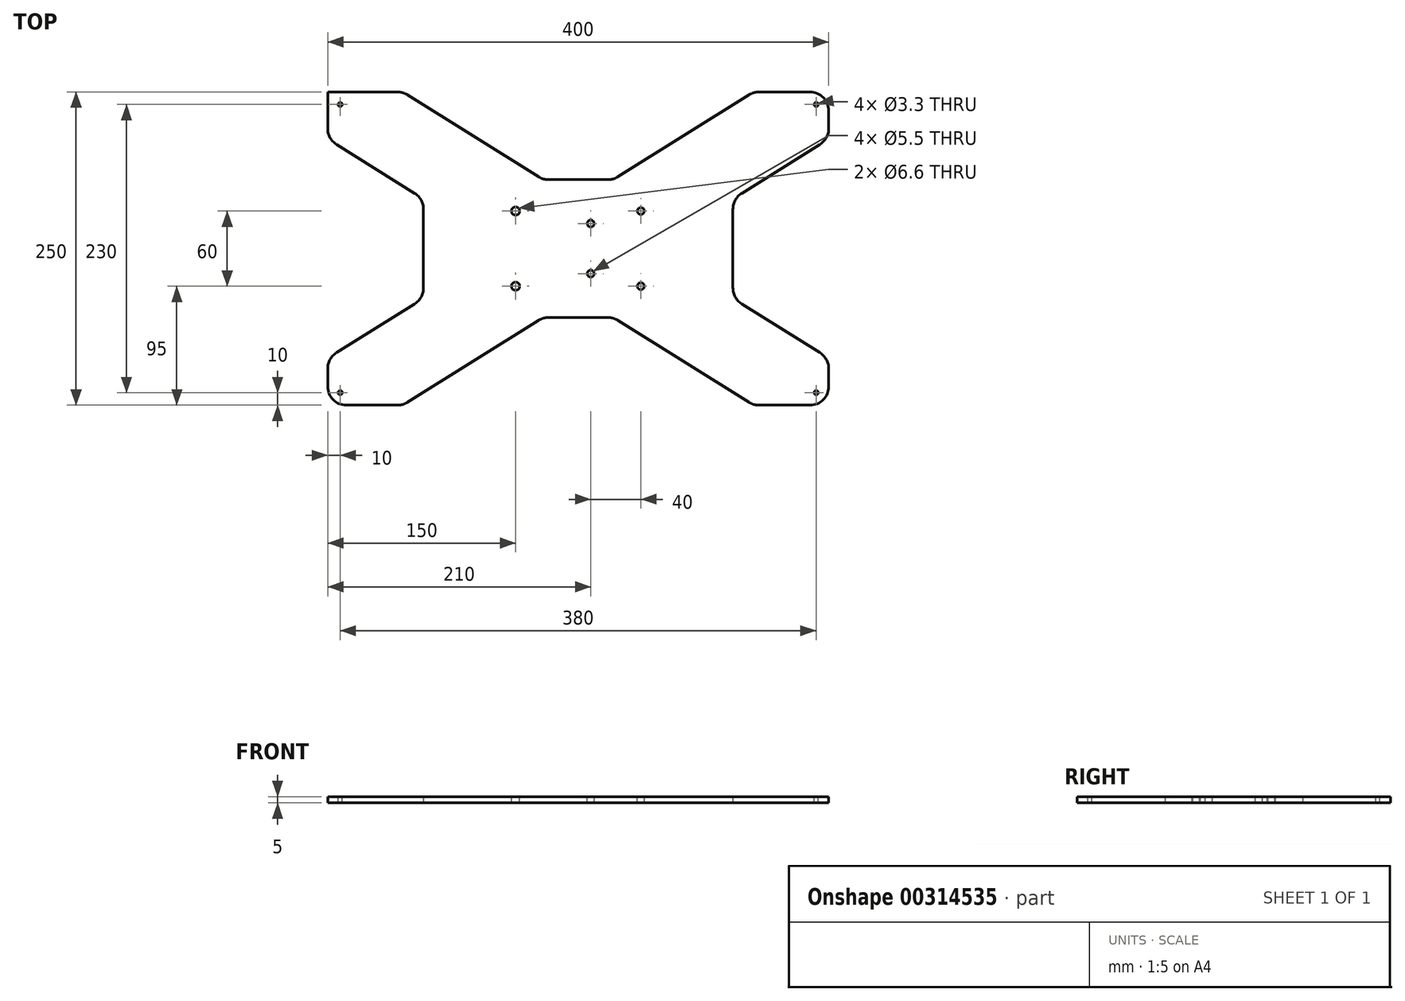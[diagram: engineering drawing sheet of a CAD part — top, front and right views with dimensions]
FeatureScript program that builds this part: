
annotation { "Feature Type Name" : "Feature", "Feature Type Description" : "" }
export const myFeature = defineFeature(function(context is Context, id is Id, definition is map)
    precondition{}
    {
        {
            var Q0;
            Q0=qCreatedBy(makeId("Top.planeOp"),FACE);
            var sketch = newSketch(context, id + "F0", { "sketchPlane" : qUnion([Q0])});
            skLineSegment(sketch, "E0.bottom", {"start": v(200, -125) * mm, "end": v(140, -125) * mm});
            skLineSegment(sketch, "E0.top", {"start": v(200, 125) * mm, "end": v(140, 125) * mm});
            skLineSegment(sketch, "E0.left", {"start": v(200, -125) * mm, "end": v(200, -87.5) * mm});
            skLineSegment(sketch, "E0.right", {"start": v(-200, -125) * mm, "end": v(-200, -87.5) * mm});
            skPoint(sketch, "E0.middle", {"position": v(0, 0) * mm});
            skLineSegment(sketch, "E1.bottom", {"start": v(-28, -55) * mm, "end": v(28, -55) * mm});
            skLineSegment(sketch, "E1.left", {"start": v(-123.5, -39.69) * mm, "end": v(-123.5, 39.69) * mm});
            skLineSegment(sketch, "E1.right", {"start": v(123.5, -39.69) * mm, "end": v(123.5, 39.69) * mm});
            skLineSegment(sketch, "E2", {"start": v(-200, -125) * mm, "end": v(200, 125) * mm, "construction": true});
            skLineSegment(sketch, "E3", {"start": v(-200, 125) * mm, "end": v(200, -125) * mm, "construction": true});
            skLineSegment(sketch, "E4.bottom", {"start": v(-200, -125) * mm, "end": v(-140, -125) * mm});
            skLineSegment(sketch, "E5.MirrorCS", {"start": v(-200, 125) * mm, "end": v(-140, 125) * mm});
            skLineSegment(sketch, "E6.MirrorCS", {"start": v(-200, 125) * mm, "end": v(-200, 87.5) * mm});
            skLineSegment(sketch, "E7", {"start": v(-200, 87.5) * mm, "end": v(-123.5, 39.69) * mm});
            skLineSegment(sketch, "E8", {"start": v(-140, 125) * mm, "end": v(-28, 55) * mm});
            skLineSegment(sketch, "E9", {"start": v(-200, -87.5) * mm, "end": v(-123.5, -39.69) * mm});
            skLineSegment(sketch, "E10", {"start": v(-140, -125) * mm, "end": v(-28, -55) * mm});
            skPoint(sketch, "E11.MirrorCS.end.orphan", {"position": v(-140, 87.5) * mm});
            skPoint(sketch, "E12.MirrorCS.end.orphan", {"position": v(140, 87.5) * mm});
            skPoint(sketch, "E4.top.end.orphan", {"position": v(-140, -87.5) * mm});
            skPoint(sketch, "E13.MirrorCS.end.orphan", {"position": v(140, -87.5) * mm});
            skLineSegment(sketch, "E14.trimOffspring", {"start": v(123.5, 39.69) * mm, "end": v(200, 87.5) * mm});
            skLineSegment(sketch, "E15.trimOffspring", {"start": v(123.5, -39.69) * mm, "end": v(200, -87.5) * mm});
            skLineSegment(sketch, "E16.trimOffspring", {"start": v(28, 55) * mm, "end": v(140, 125) * mm});
            skLineSegment(sketch, "E17.trimOffspring", {"start": v(28, -55) * mm, "end": v(140, -125) * mm});
            skLineSegment(sketch, "E18.trimOffspring", {"start": v(-200, 87.5) * mm, "end": v(-200, 125) * mm});
            skLineSegment(sketch, "E19.trimOffspring", {"start": v(-140, 125) * mm, "end": v(-200, 125) * mm});
            skLineSegment(sketch, "E20.trimOffspring", {"start": v(200, 87.5) * mm, "end": v(200, 125) * mm});
            skLineSegment(sketch, "E21.trimOffspring", {"start": v(-140, -125) * mm, "end": v(-200, -125) * mm});
            skPoint(sketch, "E22.orphan", {"position": v(123.5, 55) * mm});
            skLineSegment(sketch, "E23.trimOffspring", {"start": v(-28, 55) * mm, "end": v(28, 55) * mm});
            skPoint(sketch, "E24.orphan", {"position": v(-123.5, 55) * mm});
            skPoint(sketch, "E25.orphan", {"position": v(-123.5, -55) * mm});
            skPoint(sketch, "E26.orphan", {"position": v(123.5, -55) * mm});
            skSolve(sketch);
        }
        {
            var Q0;
            Q0 = qSketchRegion(id + "F0", true);
            extrude(context, id + "F1", {"entities" : qUnion([Q0]), "depth" : 5 * mm});
        }
        {
            var Q0;
            Q0=makeQuery(id+"F1.opExtrude","CAP_FACE",FACE,{"disambiguationData":[OSD([sQuery(id+"F0.wireOp",EDGE,"E1.bottom"),sQuery(id+"F0.wireOp",EDGE,"E1.left"),sQuery(id+"F0.wireOp",EDGE,"E1.right"),sQuery(id+"F0.wireOp",EDGE,"E0.right"),sQuery(id+"F0.wireOp",EDGE,"E0.top"),sQuery(id+"F0.wireOp",EDGE,"E0.left"),sQuery(id+"F0.wireOp",EDGE,"E0.bottom"),sQuery(id+"F0.wireOp",EDGE,"E7"),sQuery(id+"F0.wireOp",EDGE,"E8"),sQuery(id+"F0.wireOp",EDGE,"E9"),sQuery(id+"F0.wireOp",EDGE,"E10"),sQuery(id+"F0.wireOp",EDGE,"E14.trimOffspring"),sQuery(id+"F0.wireOp",EDGE,"E15.trimOffspring"),sQuery(id+"F0.wireOp",EDGE,"E16.trimOffspring"),sQuery(id+"F0.wireOp",EDGE,"E17.trimOffspring"),sQuery(id+"F0.wireOp",EDGE,"E18.trimOffspring"),sQuery(id+"F0.wireOp",EDGE,"E19.trimOffspring"),sQuery(id+"F0.wireOp",EDGE,"E21.trimOffspring"),sQuery(id+"F0.wireOp",EDGE,"E20.trimOffspring"),sQuery(id+"F0.wireOp",EDGE,"E23.trimOffspring")])],"isStart":false});
            var sketch = newSketch(context, id + "F2", { "sketchPlane" : qUnion([Q0])});
            skPoint(sketch, "E27", {"position": v(-190, 115) * mm});
            skPoint(sketch, "E28.0.1.0", {"position": v(-190, -115) * mm});
            skPoint(sketch, "E28.1.0.0", {"position": v(190, 115) * mm});
            skPoint(sketch, "E28.1.1.0", {"position": v(190, -115) * mm});
            skLineSegment(sketch, "E28.direction1", {"start": v(-190, 115) * mm, "end": v(190, 115) * mm, "construction": true});
            skLineSegment(sketch, "E28.direction2", {"start": v(-190, 115) * mm, "end": v(-190, -115) * mm, "construction": true});
            skLineSegment(sketch, "E29.bottom", {"start": v(-50, -30) * mm, "end": v(50, -30) * mm, "construction": true});
            skLineSegment(sketch, "E29.top", {"start": v(-50, 30) * mm, "end": v(50, 30) * mm, "construction": true});
            skLineSegment(sketch, "E29.left", {"start": v(-50, -30) * mm, "end": v(-50, 30) * mm, "construction": true});
            skLineSegment(sketch, "E29.right", {"start": v(50, -30) * mm, "end": v(50, 30) * mm, "construction": true});
            skPoint(sketch, "E29.middle", {"position": v(0, 0) * mm});
            skPoint(sketch, "E30", {"position": v(-50, 30) * mm});
            skPoint(sketch, "E31", {"position": v(-50, -30) * mm});
            skPoint(sketch, "E32", {"position": v(50, 30) * mm});
            skPoint(sketch, "E33", {"position": v(50, -30) * mm});
            skPoint(sketch, "E34", {"position": v(10, -20) * mm});
            skPoint(sketch, "E35", {"position": v(10, 20) * mm});
            skSolve(sketch);
        }
        {
            var Q0;
            Q0=sQuery(id+"F2.wireOp",VERTEX,"E27");
            var Q1;
            Q1=sQuery(id+"F2.wireOp",VERTEX,"E28.0.1.0");
            var Q2;
            Q2=sQuery(id+"F2.wireOp",VERTEX,"E28.1.1.0");
            var Q3;
            Q3=sQuery(id+"F2.wireOp",VERTEX,"E28.1.0.0");
            var Q4;
            Q4=makeQuery(id+"F1.opExtrude","SWEPT_BODY",BODY,{"disambiguationData":[OSD([sQuery(id+"F0.wireOp",EDGE,"E1.bottom"),sQuery(id+"F0.wireOp",EDGE,"E1.left"),sQuery(id+"F0.wireOp",EDGE,"E1.right"),sQuery(id+"F0.wireOp",EDGE,"E0.right"),sQuery(id+"F0.wireOp",EDGE,"E0.top"),sQuery(id+"F0.wireOp",EDGE,"E0.left"),sQuery(id+"F0.wireOp",EDGE,"E0.bottom"),sQuery(id+"F0.wireOp",EDGE,"E7"),sQuery(id+"F0.wireOp",EDGE,"E8"),sQuery(id+"F0.wireOp",EDGE,"E9"),sQuery(id+"F0.wireOp",EDGE,"E10"),sQuery(id+"F0.wireOp",EDGE,"E14.trimOffspring"),sQuery(id+"F0.wireOp",EDGE,"E15.trimOffspring"),sQuery(id+"F0.wireOp",EDGE,"E16.trimOffspring"),sQuery(id+"F0.wireOp",EDGE,"E17.trimOffspring"),sQuery(id+"F0.wireOp",EDGE,"E18.trimOffspring"),sQuery(id+"F0.wireOp",EDGE,"E19.trimOffspring"),sQuery(id+"F0.wireOp",EDGE,"E21.trimOffspring"),sQuery(id+"F0.wireOp",EDGE,"E20.trimOffspring"),sQuery(id+"F0.wireOp",EDGE,"E23.trimOffspring")])]});
            hole(context, id + "F3", {"style" : HoleStyle.SIMPLE, "endStyle" : HoleEndStyle.BLIND, "standardTappedOrClearance" : lookupTablePath({ "standard" : "ISO", "fit" : "Normal", "size" : "M3", "type" : "Clearance" }), "standardBlindInLast" : lookupTablePath({ "fit" : "Standard", "standard" : "ISO", "size" : "M3", "type" : "Clearance" }), "holeDiameter" : 3.3 * mm, "holeDepth" : 13.8 * mm, "tappedDepth" : 12 * mm, "tapClearance" : 3, "locations" : qUnion([Q0, Q1, Q2, Q3]), "scope" : qUnion([Q4])});
        }
        {
            var Q0;
            Q0=sQuery(id+"F2.wireOp",VERTEX,"E33");
            var Q1;
            Q1=sQuery(id+"F2.wireOp",VERTEX,"E32");
            var Q2;
            Q2=sQuery(id+"F2.wireOp",VERTEX,"E35");
            var Q3;
            Q3=sQuery(id+"F2.wireOp",VERTEX,"E34");
            var Q4;
            Q4=makeQuery(id+"F1.opExtrude","SWEPT_BODY",BODY,{"disambiguationData":[OSD([sQuery(id+"F0.wireOp",EDGE,"E1.bottom"),sQuery(id+"F0.wireOp",EDGE,"E1.left"),sQuery(id+"F0.wireOp",EDGE,"E1.right"),sQuery(id+"F0.wireOp",EDGE,"E0.right"),sQuery(id+"F0.wireOp",EDGE,"E0.top"),sQuery(id+"F0.wireOp",EDGE,"E0.left"),sQuery(id+"F0.wireOp",EDGE,"E0.bottom"),sQuery(id+"F0.wireOp",EDGE,"E7"),sQuery(id+"F0.wireOp",EDGE,"E8"),sQuery(id+"F0.wireOp",EDGE,"E9"),sQuery(id+"F0.wireOp",EDGE,"E10"),sQuery(id+"F0.wireOp",EDGE,"E14.trimOffspring"),sQuery(id+"F0.wireOp",EDGE,"E15.trimOffspring"),sQuery(id+"F0.wireOp",EDGE,"E16.trimOffspring"),sQuery(id+"F0.wireOp",EDGE,"E17.trimOffspring"),sQuery(id+"F0.wireOp",EDGE,"E18.trimOffspring"),sQuery(id+"F0.wireOp",EDGE,"E19.trimOffspring"),sQuery(id+"F0.wireOp",EDGE,"E21.trimOffspring"),sQuery(id+"F0.wireOp",EDGE,"E20.trimOffspring"),sQuery(id+"F0.wireOp",EDGE,"E23.trimOffspring")])]});
            hole(context, id + "F4", {"style" : HoleStyle.SIMPLE, "endStyle" : HoleEndStyle.BLIND, "standardTappedOrClearance" : lookupTablePath({ "standard" : "ISO", "fit" : "Normal", "size" : "M5", "type" : "Clearance" }), "standardBlindInLast" : lookupTablePath({ "fit" : "Standard", "standard" : "ISO", "size" : "M5", "type" : "Clearance" }), "holeDiameter" : 5.5 * mm, "holeDepth" : 13.8 * mm, "tappedDepth" : 12 * mm, "tapClearance" : 3, "locations" : qUnion([Q0, Q1, Q2, Q3]), "scope" : qUnion([Q4])});
        }
        {
            var Q0;
            Q0=sQuery(id+"F2.wireOp",VERTEX,"E30");
            var Q1;
            Q1=sQuery(id+"F2.wireOp",VERTEX,"E31");
            var Q2;
            Q2=makeQuery(id+"F1.opExtrude","SWEPT_BODY",BODY,{"disambiguationData":[OSD([sQuery(id+"F0.wireOp",EDGE,"E1.bottom"),sQuery(id+"F0.wireOp",EDGE,"E1.left"),sQuery(id+"F0.wireOp",EDGE,"E1.right"),sQuery(id+"F0.wireOp",EDGE,"E0.right"),sQuery(id+"F0.wireOp",EDGE,"E0.top"),sQuery(id+"F0.wireOp",EDGE,"E0.left"),sQuery(id+"F0.wireOp",EDGE,"E0.bottom"),sQuery(id+"F0.wireOp",EDGE,"E7"),sQuery(id+"F0.wireOp",EDGE,"E8"),sQuery(id+"F0.wireOp",EDGE,"E9"),sQuery(id+"F0.wireOp",EDGE,"E10"),sQuery(id+"F0.wireOp",EDGE,"E14.trimOffspring"),sQuery(id+"F0.wireOp",EDGE,"E15.trimOffspring"),sQuery(id+"F0.wireOp",EDGE,"E16.trimOffspring"),sQuery(id+"F0.wireOp",EDGE,"E17.trimOffspring"),sQuery(id+"F0.wireOp",EDGE,"E18.trimOffspring"),sQuery(id+"F0.wireOp",EDGE,"E19.trimOffspring"),sQuery(id+"F0.wireOp",EDGE,"E21.trimOffspring"),sQuery(id+"F0.wireOp",EDGE,"E20.trimOffspring"),sQuery(id+"F0.wireOp",EDGE,"E23.trimOffspring")])]});
            hole(context, id + "F5", {"style" : HoleStyle.SIMPLE, "endStyle" : HoleEndStyle.BLIND, "standardTappedOrClearance" : lookupTablePath({ "standard" : "ISO", "fit" : "Normal", "size" : "M6", "type" : "Clearance" }), "standardBlindInLast" : lookupTablePath({ "fit" : "Standard", "standard" : "ISO", "size" : "M6", "type" : "Clearance" }), "holeDiameter" : 6.6 * mm, "holeDepth" : 13.8 * mm, "tappedDepth" : 12 * mm, "tapClearance" : 3, "locations" : qUnion([Q0, Q1]), "scope" : qUnion([Q2])});
        }
        {
            var Q0;
            Q0=makeQuery(id+"F1.opExtrude","SWEPT_EDGE",EDGE,{"disambiguationData":[OSD([sQuery(id+"F0.wireOp",EDGE,"E1.bottom"),sQuery(id+"F0.wireOp",EDGE,"E10")])]});
            var Q1;
            Q1=makeQuery(id+"F1.opExtrude","SWEPT_EDGE",EDGE,{"disambiguationData":[OSD([sQuery(id+"F0.wireOp",EDGE,"E1.bottom"),sQuery(id+"F0.wireOp",EDGE,"E17.trimOffspring")])]});
            var Q2;
            Q2=makeQuery(id+"F1.opExtrude","SWEPT_EDGE",EDGE,{"disambiguationData":[OSD([sQuery(id+"F0.wireOp",EDGE,"E0.bottom"),sQuery(id+"F0.wireOp",EDGE,"E17.trimOffspring")])]});
            var Q3;
            Q3=makeQuery(id+"F1.opExtrude","SWEPT_EDGE",EDGE,{"disambiguationData":[OSD([sQuery(id+"F0.wireOp",EDGE,"E0.left"),sQuery(id+"F0.wireOp",EDGE,"E0.bottom")])]});
            var Q4;
            Q4=makeQuery(id+"F1.opExtrude","SWEPT_EDGE",EDGE,{"disambiguationData":[OSD([sQuery(id+"F0.wireOp",EDGE,"E0.left"),sQuery(id+"F0.wireOp",EDGE,"E15.trimOffspring")])]});
            var Q5;
            Q5=makeQuery(id+"F1.opExtrude","SWEPT_EDGE",EDGE,{"disambiguationData":[OSD([sQuery(id+"F0.wireOp",EDGE,"E1.right"),sQuery(id+"F0.wireOp",EDGE,"E15.trimOffspring")])]});
            var Q6;
            Q6=makeQuery(id+"F1.opExtrude","SWEPT_EDGE",EDGE,{"disambiguationData":[OSD([sQuery(id+"F0.wireOp",EDGE,"E1.right"),sQuery(id+"F0.wireOp",EDGE,"E14.trimOffspring")])]});
            var Q7;
            Q7=makeQuery(id+"F1.opExtrude","SWEPT_EDGE",EDGE,{"disambiguationData":[OSD([sQuery(id+"F0.wireOp",EDGE,"E14.trimOffspring"),sQuery(id+"F0.wireOp",EDGE,"E20.trimOffspring")])]});
            var Q8;
            Q8=makeQuery(id+"F1.opExtrude","SWEPT_EDGE",EDGE,{"disambiguationData":[OSD([sQuery(id+"F0.wireOp",EDGE,"E0.top"),sQuery(id+"F0.wireOp",EDGE,"E20.trimOffspring")])]});
            var Q9;
            Q9=makeQuery(id+"F1.opExtrude","SWEPT_EDGE",EDGE,{"disambiguationData":[OSD([sQuery(id+"F0.wireOp",EDGE,"E0.top"),sQuery(id+"F0.wireOp",EDGE,"E16.trimOffspring")])]});
            var Q10;
            Q10=makeQuery(id+"F1.opExtrude","SWEPT_EDGE",EDGE,{"disambiguationData":[OSD([sQuery(id+"F0.wireOp",EDGE,"E16.trimOffspring"),sQuery(id+"F0.wireOp",EDGE,"E23.trimOffspring")])]});
            var Q11;
            Q11=makeQuery(id+"F1.opExtrude","SWEPT_EDGE",EDGE,{"disambiguationData":[OSD([sQuery(id+"F0.wireOp",EDGE,"E8"),sQuery(id+"F0.wireOp",EDGE,"E23.trimOffspring")])]});
            var Q12;
            Q12=makeQuery(id+"F1.opExtrude","SWEPT_EDGE",EDGE,{"disambiguationData":[OSD([sQuery(id+"F0.wireOp",EDGE,"E8"),sQuery(id+"F0.wireOp",EDGE,"E19.trimOffspring")])]});
            var Q13;
            Q13=makeQuery(id+"F1.opExtrude","SWEPT_EDGE",EDGE,{"disambiguationData":[OSD([sQuery(id+"F0.wireOp",EDGE,"E18.trimOffspring"),sQuery(id+"F0.wireOp",EDGE,"E19.trimOffspring")])]});
            var Q14;
            Q14=makeQuery(id+"F1.opExtrude","SWEPT_EDGE",EDGE,{"disambiguationData":[OSD([sQuery(id+"F0.wireOp",EDGE,"E7"),sQuery(id+"F0.wireOp",EDGE,"E18.trimOffspring")])]});
            var Q15;
            Q15=makeQuery(id+"F1.opExtrude","SWEPT_EDGE",EDGE,{"disambiguationData":[OSD([sQuery(id+"F0.wireOp",EDGE,"E1.left"),sQuery(id+"F0.wireOp",EDGE,"E7")])]});
            var Q16;
            Q16=makeQuery(id+"F1.opExtrude","SWEPT_EDGE",EDGE,{"disambiguationData":[OSD([sQuery(id+"F0.wireOp",EDGE,"E1.left"),sQuery(id+"F0.wireOp",EDGE,"E9")])]});
            var Q17;
            Q17=makeQuery(id+"F1.opExtrude","SWEPT_EDGE",EDGE,{"disambiguationData":[OSD([sQuery(id+"F0.wireOp",EDGE,"E0.right"),sQuery(id+"F0.wireOp",EDGE,"E9")])]});
            var Q18;
            Q18=makeQuery(id+"F1.opExtrude","SWEPT_EDGE",EDGE,{"disambiguationData":[OSD([sQuery(id+"F0.wireOp",EDGE,"E0.right"),sQuery(id+"F0.wireOp",EDGE,"E21.trimOffspring")])]});
            var Q19;
            Q19=makeQuery(id+"F1.opExtrude","SWEPT_EDGE",EDGE,{"disambiguationData":[OSD([sQuery(id+"F0.wireOp",EDGE,"E10"),sQuery(id+"F0.wireOp",EDGE,"E21.trimOffspring")])]});
            fillet(context, id + "F6", {"entities" : qUnion([Q0, Q1, Q2, Q3, Q4, Q5, Q6, Q7, Q8, Q9, Q10, Q11, Q12, Q13, Q14, Q15, Q16, Q17, Q18, Q19]), "radius" : 15 * mm, "tangentPropagation" : true, "allowEdgeOverflow" : false});
        }
    });
